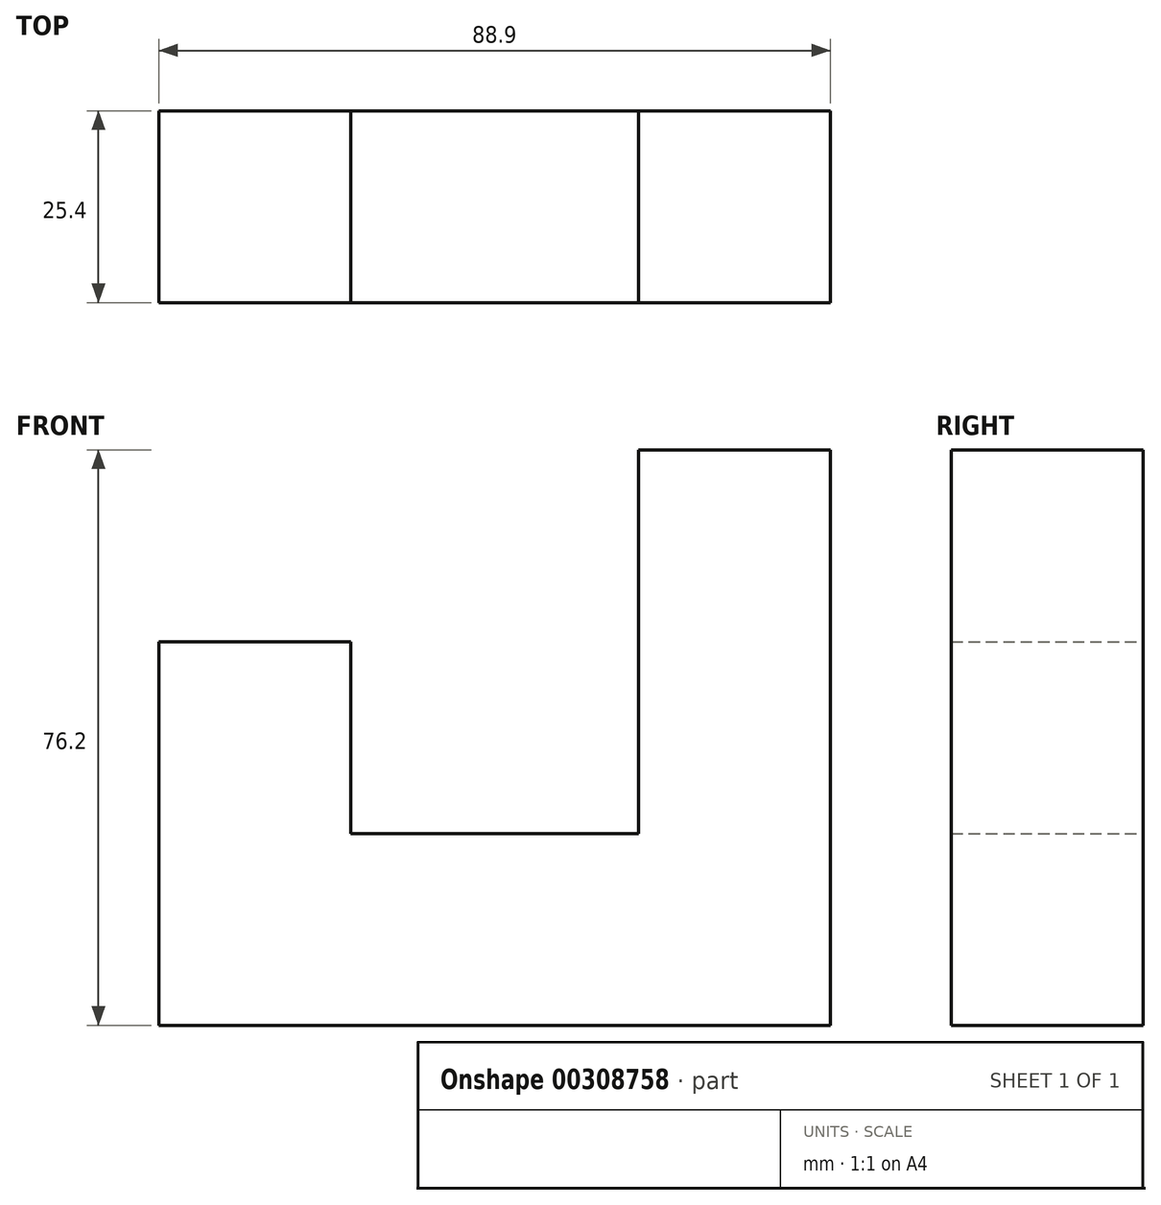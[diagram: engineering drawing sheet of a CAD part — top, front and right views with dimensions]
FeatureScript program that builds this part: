
annotation { "Feature Type Name" : "Feature", "Feature Type Description" : "" }
export const myFeature = defineFeature(function(context is Context, id is Id, definition is map)
    precondition{}
    {
        {
            var Q0;
            Q0=qCreatedBy(makeId("Front.planeOp"),FACE);
            var sketch = newSketch(context, id + "F0", { "sketchPlane" : qUnion([Q0])});
            skLineSegment(sketch, "E0", {"start": v(-41.74, -59.15) * mm, "end": v(47.16, -59.15) * mm});
            skLineSegment(sketch, "E1", {"start": v(47.16, -59.15) * mm, "end": v(47.16, 17.05) * mm});
            skLineSegment(sketch, "E2", {"start": v(47.16, 17.05) * mm, "end": v(21.76, 17.05) * mm});
            skLineSegment(sketch, "E3", {"start": v(21.76, 17.05) * mm, "end": v(21.76, -33.75) * mm});
            skLineSegment(sketch, "E4", {"start": v(21.76, -33.75) * mm, "end": v(-16.34, -33.75) * mm});
            skLineSegment(sketch, "E5", {"start": v(-16.34, -33.75) * mm, "end": v(-16.34, -8.35) * mm});
            skLineSegment(sketch, "E6", {"start": v(-16.34, -8.35) * mm, "end": v(-41.74, -8.35) * mm});
            skLineSegment(sketch, "E7", {"start": v(-41.74, -8.35) * mm, "end": v(-41.74, -59.15) * mm});
            skSolve(sketch);
        }
        {
            var Q0;
            Q0=makeQuery(id+"F0.imprint","IMPRINT",FACE,{"disambiguationData":[TD([[makeQuery(id+"F0.imprint","IMPRINT",EDGE,{"derivedFrom":sQuery(id+"F0.wireOp",EDGE,"E0")}),1.0]])]});
            extrude(context, id + "F1", {"entities" : qUnion([Q0]), "depth" : 25.4 * mm});
        }
    });
